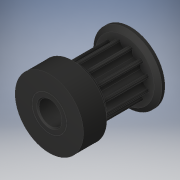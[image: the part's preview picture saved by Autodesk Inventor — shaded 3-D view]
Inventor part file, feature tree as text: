
AUTODESK INVENTOR PART (.ipt)
format: ipt  version: 2017 (Build 210142000, 142)  size: 226,304 bytes
history: native  units: in
note: dims shown in document units (in); Inventor stores cm internally (conversion verified against a paired STEP export)
features: chamfer x1
ambient origin geometry x8: Origin, YZ Plane, XZ Plane, XY Plane, X Axis, Y Axis, Z Axis, Center Point
bodies: Solid1 (feature_tree)
feature tree (1):
  chamfer  "Chamfer1"  [1 undecoded]
note: 1 required parameter value undecoded (feature->parameter linkage not recoverable at this tier; creation-order binding heuristic only, values carry confidence <= 0.55)
